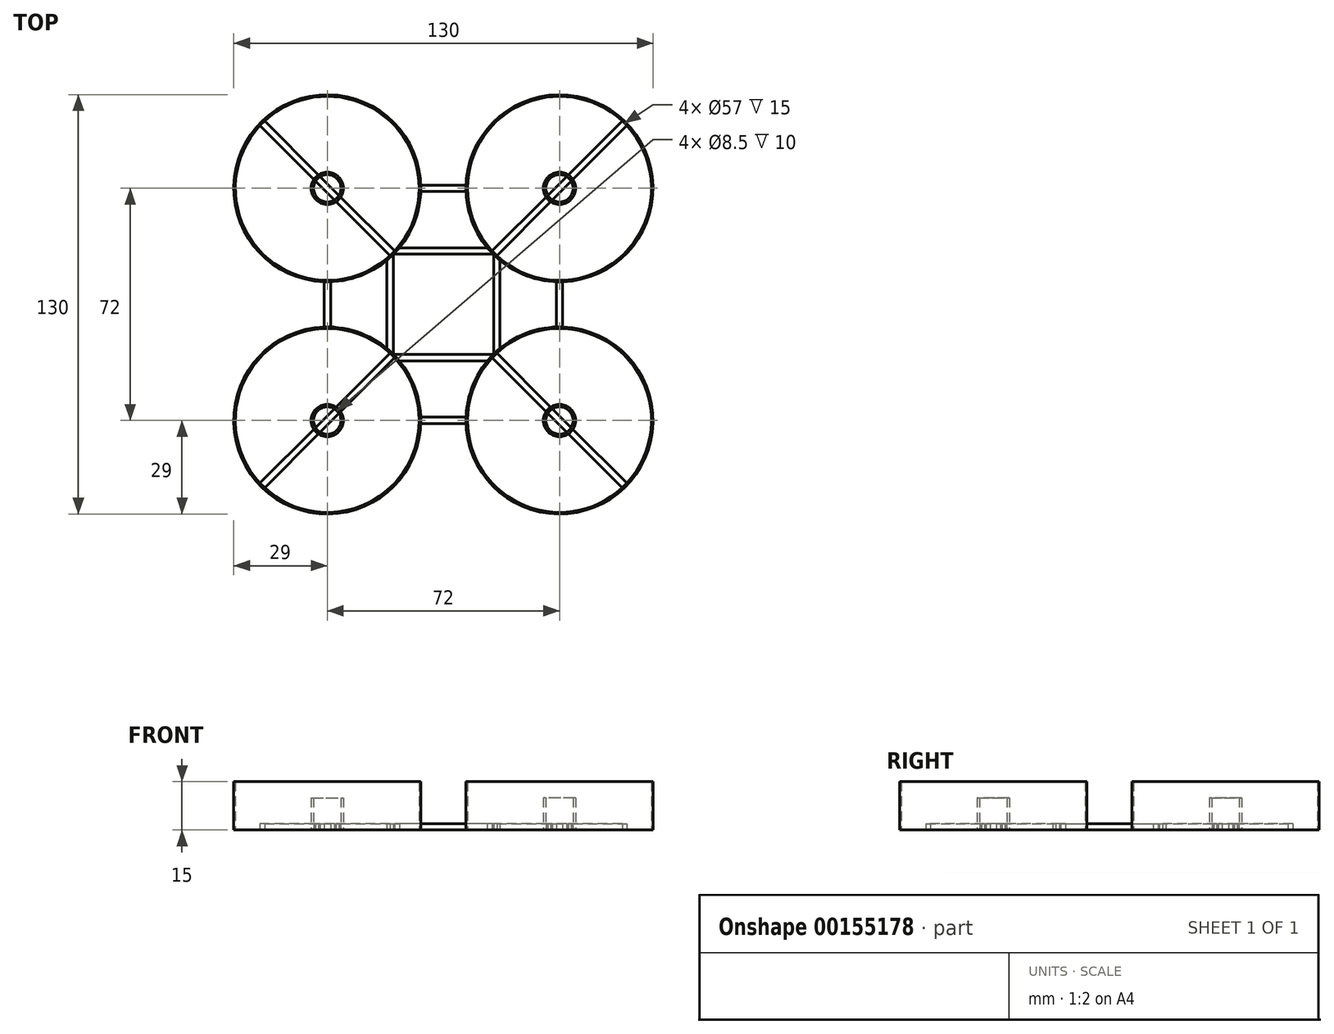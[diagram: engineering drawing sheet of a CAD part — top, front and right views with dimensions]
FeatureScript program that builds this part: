
annotation { "Feature Type Name" : "Feature", "Feature Type Description" : "" }
export const myFeature = defineFeature(function(context is Context, id is Id, definition is map)
    precondition{}
    {
        {
            var Q0;
            Q0=qCreatedBy(makeId("Top.planeOp"),FACE);
            var sketch = newSketch(context, id + "F0", { "sketchPlane" : qUnion([Q0])});
            skLineSegment(sketch, "E0", {"start": v(0, 0) * mm, "end": v(0, 36) * mm, "construction": true});
            skLineSegment(sketch, "E1", {"start": v(0, 0) * mm, "end": v(0, -36) * mm, "construction": true});
            skLineSegment(sketch, "E2", {"start": v(0, -36) * mm, "end": v(36, -36) * mm, "construction": true});
            skLineSegment(sketch, "E3", {"start": v(0, -36) * mm, "end": v(-36, -36) * mm, "construction": true});
            skLineSegment(sketch, "E4", {"start": v(0, 36) * mm, "end": v(-36, 36) * mm, "construction": true});
            skLineSegment(sketch, "E5", {"start": v(0, 36) * mm, "end": v(36, 36) * mm, "construction": true});
            skLineSegment(sketch, "E6", {"start": v(0, 0) * mm, "end": v(36, 36) * mm, "construction": true});
            skLineSegment(sketch, "E7", {"start": v(0, 0) * mm, "end": v(-36, 36) * mm, "construction": true});
            skLineSegment(sketch, "E8", {"start": v(0, 0) * mm, "end": v(-36, -36) * mm, "construction": true});
            skLineSegment(sketch, "E9", {"start": v(0, 0) * mm, "end": v(36, -36) * mm, "construction": true});
            skLineSegment(sketch, "E10", {"start": v(-36, 36) * mm, "end": v(-36, -36) * mm, "construction": true});
            skLineSegment(sketch, "E11", {"start": v(36, 36) * mm, "end": v(36, -36) * mm, "construction": true});
            skSolve(sketch);
        }
        {
            var Q0;
            Q0=qCreatedBy(makeId("Top.planeOp"),FACE);
            var sketch = newSketch(context, id + "F1", { "sketchPlane" : qUnion([Q0])});
            skLineSegment(sketch, "E12.0", {"start": v(0, 0) * mm, "end": v(-36, 36) * mm, "construction": true});
            skLineSegment(sketch, "E12.1", {"start": v(0, 36) * mm, "end": v(-36, 36) * mm, "construction": true});
            skLineSegment(sketch, "E12.2", {"start": v(0, 36) * mm, "end": v(36, 36) * mm, "construction": true});
            skLineSegment(sketch, "E12.3", {"start": v(0, 0) * mm, "end": v(36, 36) * mm, "construction": true});
            skLineSegment(sketch, "E12.4", {"start": v(0, 0) * mm, "end": v(36, -36) * mm, "construction": true});
            skLineSegment(sketch, "E12.5", {"start": v(0, -36) * mm, "end": v(36, -36) * mm, "construction": true});
            skLineSegment(sketch, "E12.6", {"start": v(0, -36) * mm, "end": v(-36, -36) * mm, "construction": true});
            skLineSegment(sketch, "E12.7", {"start": v(0, 0) * mm, "end": v(-36, -36) * mm, "construction": true});
            skCircle(sketch, "E13", {"center": v(-36, 36) * mm, "radius": 29 * mm});
            skCircle(sketch, "E14", {"center": v(-36, 36) * mm, "radius": 28.5 * mm});
            skSolve(sketch);
        }
        {
            var Q0;
            Q0 = qSketchRegion(id + "F1", true);
            extrude(context, id + "F2", {"entities" : qUnion([Q0]), "depth" : 15 * mm});
        }
        {
            var Q0;
            Q0=qCreatedBy(makeId("Top.planeOp"),FACE);
            var sketch = newSketch(context, id + "F3", { "sketchPlane" : qUnion([Q0])});
            skCircle(sketch, "E15.0", {"center": v(-36, 36) * mm, "radius": 28.5 * mm, "construction": true});
            skLineSegment(sketch, "E15.8", {"start": v(0, 0) * mm, "end": v(-36, 36) * mm});
            skLineSegment(sketch, "E15.10", {"start": v(0, 36) * mm, "end": v(-36, 36) * mm});
            skLineSegment(sketch, "E16", {"start": v(0, 0) * mm, "end": v(0.7, 0.7) * mm, "construction": true});
            skLineSegment(sketch, "E17", {"start": v(0, 0) * mm, "end": v(-0.7, -0.7) * mm, "construction": true});
            skLineSegment(sketch, "E18", {"start": v(-36, 36) * mm, "end": v(-35.3, 36.7) * mm, "construction": true});
            skLineSegment(sketch, "E19", {"start": v(-36, 36) * mm, "end": v(-36.7, 35.3) * mm, "construction": true});
            skLineSegment(sketch, "E20", {"start": v(0.7, 0.7) * mm, "end": v(-35.3, 36.7) * mm, "construction": true});
            skLineSegment(sketch, "E21", {"start": v(-0.7, -0.7) * mm, "end": v(-36.7, 35.3) * mm, "construction": true});
            skLineSegment(sketch, "E22", {"start": v(0, 36) * mm, "end": v(0, 37) * mm, "construction": true});
            skLineSegment(sketch, "E23", {"start": v(0, 36) * mm, "end": v(0, 35) * mm, "construction": true});
            skLineSegment(sketch, "E24.0", {"start": v(-36, 36) * mm, "end": v(-36, -36) * mm, "construction": true});
            skPoint(sketch, "E25", {"position": v(-36, 0) * mm});
            skLineSegment(sketch, "E26", {"start": v(-36, 0) * mm, "end": v(-35, 0) * mm, "construction": true});
            skLineSegment(sketch, "E27", {"start": v(-36, 0) * mm, "end": v(-37, 0) * mm, "construction": true});
            skCircle(sketch, "E28.0", {"center": v(-36, 36) * mm, "radius": 29 * mm, "construction": true});
            skLineSegment(sketch, "E29", {"start": v(-37, 0) * mm, "end": v(-37, 7.02) * mm});
            skLineSegment(sketch, "E30", {"start": v(-35, 0) * mm, "end": v(-35, 7.02) * mm});
            skLineSegment(sketch, "E31", {"start": v(0, 35) * mm, "end": v(-7.02, 35) * mm});
            skLineSegment(sketch, "E32", {"start": v(0, 37) * mm, "end": v(-7.02, 37) * mm});
            skLineSegment(sketch, "E33", {"start": v(0, 37) * mm, "end": v(0, 35) * mm});
            skLineSegment(sketch, "E34", {"start": v(-35, 0) * mm, "end": v(-37, 0) * mm});
            skLineSegment(sketch, "E35", {"start": v(-7.02, 37) * mm, "end": v(-7.02, 35) * mm});
            skLineSegment(sketch, "E36", {"start": v(-37, 7.02) * mm, "end": v(-35, 7.02) * mm});
            skLineSegment(sketch, "E37", {"start": v(0, 0) * mm, "end": v(-36, 0) * mm, "construction": true});
            skLineSegment(sketch, "E38", {"start": v(-16.55, 15.17) * mm, "end": v(-16.55, 0) * mm, "construction": true});
            skLineSegment(sketch, "E39", {"start": v(-16.55, 0) * mm, "end": v(-17.55, 0) * mm, "construction": true});
            skLineSegment(sketch, "E40", {"start": v(-16.55, 0) * mm, "end": v(-15.55, 0) * mm, "construction": true});
            skLineSegment(sketch, "E41", {"start": v(-17.55, 0) * mm, "end": v(-17.55, 13.63) * mm});
            skLineSegment(sketch, "E42", {"start": v(-15.55, 0) * mm, "end": v(-15.55, 15.44) * mm});
            skLineSegment(sketch, "E43", {"start": v(-15.55, 15.44) * mm, "end": v(-17.55, 13.63) * mm});
            skLineSegment(sketch, "E44", {"start": v(-15.55, 0) * mm, "end": v(-17.55, 0) * mm});
            skLineSegment(sketch, "E45", {"start": v(0, 0) * mm, "end": v(0, 36) * mm, "construction": true});
            skLineSegment(sketch, "E46", {"start": v(-15.17, 16.55) * mm, "end": v(0, 16.55) * mm, "construction": true});
            skLineSegment(sketch, "E47", {"start": v(0, 16.55) * mm, "end": v(0, 17.55) * mm, "construction": true});
            skLineSegment(sketch, "E48", {"start": v(0, 16.55) * mm, "end": v(0, 15.55) * mm, "construction": true});
            skLineSegment(sketch, "E49", {"start": v(0, 17.55) * mm, "end": v(-13.63, 17.55) * mm});
            skLineSegment(sketch, "E50", {"start": v(0, 15.55) * mm, "end": v(-15.44, 15.55) * mm});
            skLineSegment(sketch, "E51", {"start": v(-15.44, 15.55) * mm, "end": v(-13.63, 17.55) * mm});
            skLineSegment(sketch, "E52", {"start": v(0, 17.55) * mm, "end": v(0, 15.55) * mm});
            skLineSegment(sketch, "E53", {"start": v(-35.3, 36.7) * mm, "end": v(-55.62, 57.04) * mm});
            skLineSegment(sketch, "E54", {"start": v(-36.7, 35.3) * mm, "end": v(-57.04, 55.62) * mm});
            skLineSegment(sketch, "E55", {"start": v(-55.62, 57.04) * mm, "end": v(-57.04, 55.62) * mm});
            skLineSegment(sketch, "E56", {"start": v(-35.3, 36.7) * mm, "end": v(-14.96, 16.38) * mm});
            skLineSegment(sketch, "E57", {"start": v(-36.7, 35.3) * mm, "end": v(-16.38, 14.96) * mm});
            skLineSegment(sketch, "E58", {"start": v(-14.96, 16.38) * mm, "end": v(-16.38, 14.96) * mm});
            skSolve(sketch);
        }
        {
            var Q0;
            Q0 = qSketchRegion(id + "F3", true);
            extrude(context, id + "F4", {"entities" : qUnion([Q0]), "operationType" : NewBodyOperationType.ADD, "depth" : 2 * mm});
        }
        {
            var Q0;
            Q0=makeQuery(id+"F4.boolean.opBoolean","MERGE",FACE,{"derivedFrom":[makeQuery(id+"F2.opExtrude","CAP_FACE",FACE,{"disambiguationData":[OSD([sQuery(id+"F1.wireOp",EDGE,"E13"),sQuery(id+"F1.wireOp",EDGE,"E14")])],"isStart":true}),makeQuery(id+"F4.opExtrude","CAP_FACE",FACE,{"disambiguationData":[OSD([sQuery(id+"F3.wireOp",EDGE,"E29"),sQuery(id+"F3.wireOp",EDGE,"E30"),sQuery(id+"F3.wireOp",EDGE,"E34"),sQuery(id+"F3.wireOp",EDGE,"E36")])],"isStart":true}),makeQuery(id+"F4.opExtrude","CAP_FACE",FACE,{"disambiguationData":[OSD([sQuery(id+"F3.wireOp",EDGE,"E31"),sQuery(id+"F3.wireOp",EDGE,"E32"),sQuery(id+"F3.wireOp",EDGE,"E33"),sQuery(id+"F3.wireOp",EDGE,"E35")])],"isStart":true}),makeQuery(id+"F4.opExtrude","CAP_FACE",FACE,{"disambiguationData":[OSD([sQuery(id+"F3.wireOp",EDGE,"E41"),sQuery(id+"F3.wireOp",EDGE,"E42"),sQuery(id+"F3.wireOp",EDGE,"E43"),sQuery(id+"F3.wireOp",EDGE,"E44")])],"isStart":true}),makeQuery(id+"F4.opExtrude","CAP_FACE",FACE,{"disambiguationData":[OSD([sQuery(id+"F3.wireOp",EDGE,"E49"),sQuery(id+"F3.wireOp",EDGE,"E50"),sQuery(id+"F3.wireOp",EDGE,"E51"),sQuery(id+"F3.wireOp",EDGE,"E52")])],"isStart":true}),makeQuery(id+"F4.opExtrude","CAP_FACE",FACE,{"disambiguationData":[OSD([sQuery(id+"F3.wireOp",EDGE,"E53"),sQuery(id+"F3.wireOp",EDGE,"E54"),sQuery(id+"F3.wireOp",EDGE,"E55"),sQuery(id+"F3.wireOp",EDGE,"E56"),sQuery(id+"F3.wireOp",EDGE,"E57"),sQuery(id+"F3.wireOp",EDGE,"E58")])],"isStart":true})]});
            var sketch = newSketch(context, id + "F5", { "sketchPlane" : qUnion([Q0])});
            skLineSegment(sketch, "E59.0", {"start": v(0, -36) * mm, "end": v(-36, -36) * mm, "construction": true});
            skLineSegment(sketch, "E59.1", {"start": v(-36, -36) * mm, "end": v(-36, 36) * mm, "construction": true});
            skLineSegment(sketch, "E59.2", {"start": v(0, 0) * mm, "end": v(-36, -36) * mm, "construction": true});
            skCircle(sketch, "E60", {"center": v(-36, -36) * mm, "radius": 5 * mm});
            skCircle(sketch, "E61", {"center": v(-36, -36) * mm, "radius": 4.25 * mm});
            skSolve(sketch);
        }
        {
            var Q0;
            Q0 = qSketchRegion(id + "F5", true);
            extrude(context, id + "F6", {"entities" : qUnion([Q0]), "operationType" : NewBodyOperationType.ADD, "oppositeDirection" : true, "depth" : 10 * mm});
        }
        {
            var Q0;
            Q0=qCreatedBy(makeId("Front.planeOp"),FACE);
            var sketch = newSketch(context, id + "F7", { "sketchPlane" : qUnion([Q0])});
            skLineSegment(sketch, "E62", {"start": v(0, 0) * mm, "end": v(0, 10) * mm, "construction": true});
            skSolve(sketch);
        }
        {
            var Q0;
            Q0=makeQuery(id+"F2.opExtrude","SWEPT_BODY",BODY,{"disambiguationData":[OSD([sQuery(id+"F1.wireOp",EDGE,"E13"),sQuery(id+"F1.wireOp",EDGE,"E14")])]});
            var Q1;
            Q1=qCreatedBy(makeId("Front.planeOp"),FACE);
            mirror(context, id + "F8", {"operationType" : NewBodyOperationType.ADD, "entities" : qUnion([Q0]), "mirrorPlane" : qUnion([Q1])});
        }
        {
            var Q0;
            Q0=makeQuery(id+"F2.opExtrude","SWEPT_BODY",BODY,{"disambiguationData":[OSD([sQuery(id+"F1.wireOp",EDGE,"E13"),sQuery(id+"F1.wireOp",EDGE,"E14")])]});
            var Q1;
            Q1=qCreatedBy(makeId("Right.planeOp"),FACE);
            mirror(context, id + "F9", {"operationType" : NewBodyOperationType.ADD, "entities" : qUnion([Q0]), "mirrorPlane" : qUnion([Q1])});
        }
    });
